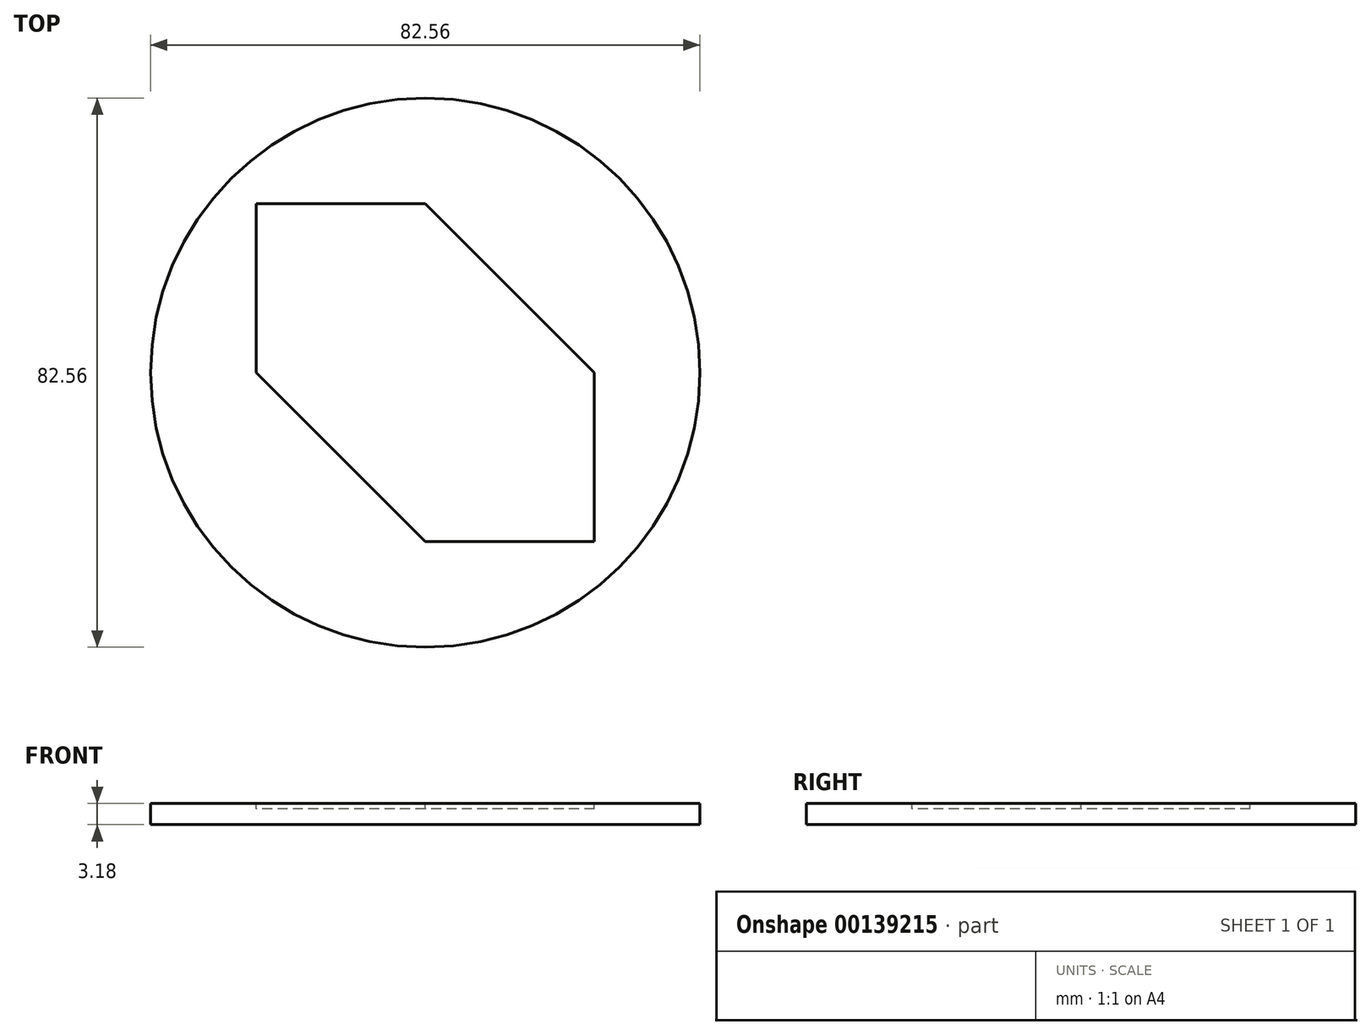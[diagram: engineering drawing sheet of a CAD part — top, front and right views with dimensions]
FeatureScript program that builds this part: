
annotation { "Feature Type Name" : "Feature", "Feature Type Description" : "" }
export const myFeature = defineFeature(function(context is Context, id is Id, definition is map)
    precondition{}
    {
        {
            var Q0;
            Q0=qCreatedBy(makeId("Top.planeOp"),FACE);
            var sketch = newSketch(context, id + "F0", { "sketchPlane" : qUnion([Q0])});
            skCircle(sketch, "E0", {"center": v(0, 0) * mm, "radius": 41.28 * mm});
            skSolve(sketch);
        }
        {
            var Q0;
            Q0=makeQuery(id+"F0.imprint","IMPRINT",FACE,{"disambiguationData":[TD([[makeQuery(id+"F0.imprint","IMPRINT",EDGE,{"derivedFrom":sQuery(id+"F0.wireOp",EDGE,"E0")}),1.0]])]});
            var Q1;
            Q1=sQuery(id+"F0.wireOp",EDGE,"E0");
            extrude(context, id + "F1", {"entities" : qUnion([Q0]), "surfaceEntities" : qUnion([Q1]), "depth" : 3.17 * mm});
        }
        {
            var Q0;
            Q0=makeQuery(id+"F1.opExtrude","CAP_FACE",FACE,{"disambiguationData":[OSD([sQuery(id+"F0.wireOp",EDGE,"E0")])],"isStart":false});
            var sketch = newSketch(context, id + "F2", { "sketchPlane" : qUnion([Q0])});
            skCircle(sketch, "E1", {"center": v(0, 0) * mm, "radius": 38.23 * mm});
            skCircle(sketch, "E2", {"center": v(0, 0) * mm, "radius": 36.86 * mm});
            skSolve(sketch);
        }
        {
            var Q0;
            Q0 = qSketchRegion(id + "F2", true);
            extrude(context, id + "F3", {"entities" : qUnion([Q0]), "operationType" : NewBodyOperationType.REMOVE, "oppositeDirection" : true, "depth" : 1 / 812.8 * mm});
        }
        {
            var Q0;
            Q0=makeQuery(id+"F3.boolean.opBoolean","SPLIT",FACE,{"disambiguationData":[TD([makeQuery(id+"F3.opExtrude","SWEPT_FACE",FACE,{"disambiguationData":[OSD([sQuery(id+"F2.wireOp",EDGE,"E2")])]})])],"derivedFrom":makeQuery(id+"F1.opExtrude","CAP_FACE",FACE,{"disambiguationData":[OSD([sQuery(id+"F0.wireOp",EDGE,"E0")])],"isStart":false})});
            var sketch = newSketch(context, id + "F4", { "sketchPlane" : qUnion([Q0])});
            skLineSegment(sketch, "E3.bottom", {"start": v(0, 25.4) * mm, "end": v(-25.4, 25.4) * mm});
            skLineSegment(sketch, "E3.top", {"start": v(25.4, -25.4) * mm, "end": v(0, -25.4) * mm});
            skLineSegment(sketch, "E3.left", {"start": v(25.4, 0) * mm, "end": v(25.4, -25.4) * mm});
            skLineSegment(sketch, "E3.right", {"start": v(-25.4, 25.4) * mm, "end": v(-25.4, 0) * mm});
            skPoint(sketch, "E3.middle", {"position": v(0, 0) * mm});
            skLineSegment(sketch, "E4", {"start": v(-25.4, 0) * mm, "end": v(0, -25.4) * mm});
            skLineSegment(sketch, "E5", {"start": v(0, 25.4) * mm, "end": v(25.4, 0) * mm});
            skPoint(sketch, "E6.orphan", {"position": v(25.4, 25.4) * mm});
            skPoint(sketch, "E7.orphan", {"position": v(-25.4, -25.4) * mm});
            skSolve(sketch);
        }
        {
            var Q0;
            Q0 = qSketchRegion(id + "F4", true);
            extrude(context, id + "F5", {"entities" : qUnion([Q0]), "operationType" : NewBodyOperationType.REMOVE, "oppositeDirection" : true, "depth" : 0.8 * mm});
        }
    });
